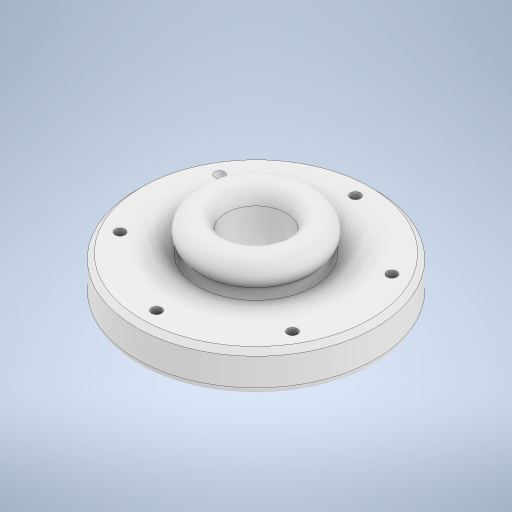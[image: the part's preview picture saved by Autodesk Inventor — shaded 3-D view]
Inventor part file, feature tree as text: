
AUTODESK INVENTOR PART (.ipt)
format: ipt  version: 2023 (Build 270158030, 158C)  size: 331,776 bytes
history: native  units: in
note: dims shown in document units (in); Inventor stores cm internally (conversion verified against a paired STEP export)
features: sketch x4, other x2, extrude x1, fillet x1, hole x1, pattern_circular x1, chamfer x1
ambient origin geometry x8: Origin, YZ Plane, XZ Plane, XY Plane, X Axis, Y Axis, Z Axis, Center Point
bodies: Solid1 (feature_tree)
feature tree (11):
  extrude  "Main-Body"  Depth=1.0in TaperAngle=0.0deg
  other  "Middle-Cutout"
  other  "Bump"
  fillet  "Fillet4"  Radius=1.0in
  hole  "Hole1"  [1 undecoded]
  pattern_circular  "Circular Pattern1"  [2 undecoded]
  chamfer  "Chamfer1"  Distance=2.5in
  sketch  "Sketch1"  dims[d0=6.0in d1=1.0in d2=0.0in d12=1.0in]
  sketch  "Sketch3"  dims[d13=360.0deg d17=360.0deg]
  sketch  "Sketch4"  dims[d19=0.75in]
  sketch  "Sketch6"  dims[d20=0.25in d22=6.1in d33=0.1875in d34=0.252in d35=0.75in d36=0.375in d37=0.25in d38=0.5635in d39=0.4173in d40=0.0in d41=2.5in d42=2.3622in d43=360.0deg d45=0.125in d46=0.125in d47=45.0deg d48=0.375in d50=0.5in d51=0.125in]
note: 3 required parameter values undecoded (feature->parameter linkage not recoverable at this tier; creation-order binding heuristic only, values carry confidence <= 0.55)
